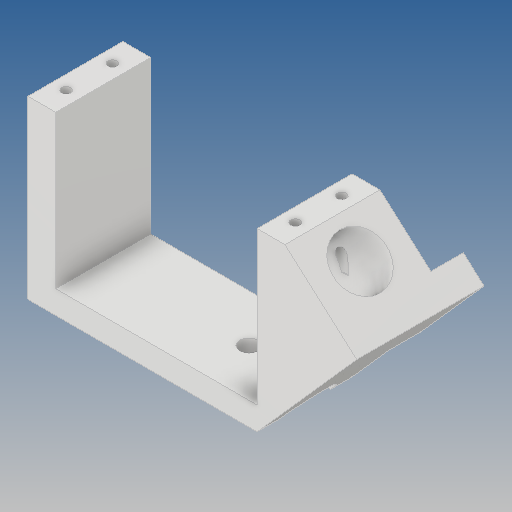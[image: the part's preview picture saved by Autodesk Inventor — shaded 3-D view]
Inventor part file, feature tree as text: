
AUTODESK INVENTOR PART (.ipt)
format: ipt  version: 2020 (Build 240168000, 168)  size: 184,832 bytes
history: native  units: mm
features: extrude x6, sketch x5, other x1
ambient origin geometry x8: Origin, YZ Plane, XZ Plane, XY Plane, X Axis, Y Axis, Z Axis, Center Point
bodies: Body1 (feature_tree)
feature tree (12):
  other  "Твердое тело1"
  extrude  "Выдавливание1"  Depth=5.0mm
  extrude  "Выдавливание2"  Depth=6.0mm
  sketch  "Эскиз3"
  extrude  "Выдавливание3"  Depth=43.5mm
  extrude  "Выдавливание4"  Depth=6.0mm
  extrude  "Выдавливание5"  Depth=38.0mm
  extrude  "Выдавливание6"  Depth=38.0mm
  sketch  "Эскиз1"
  sketch  "Эскиз2"
  sketch  "Эскиз4"
  sketch  "Эскиз5"
